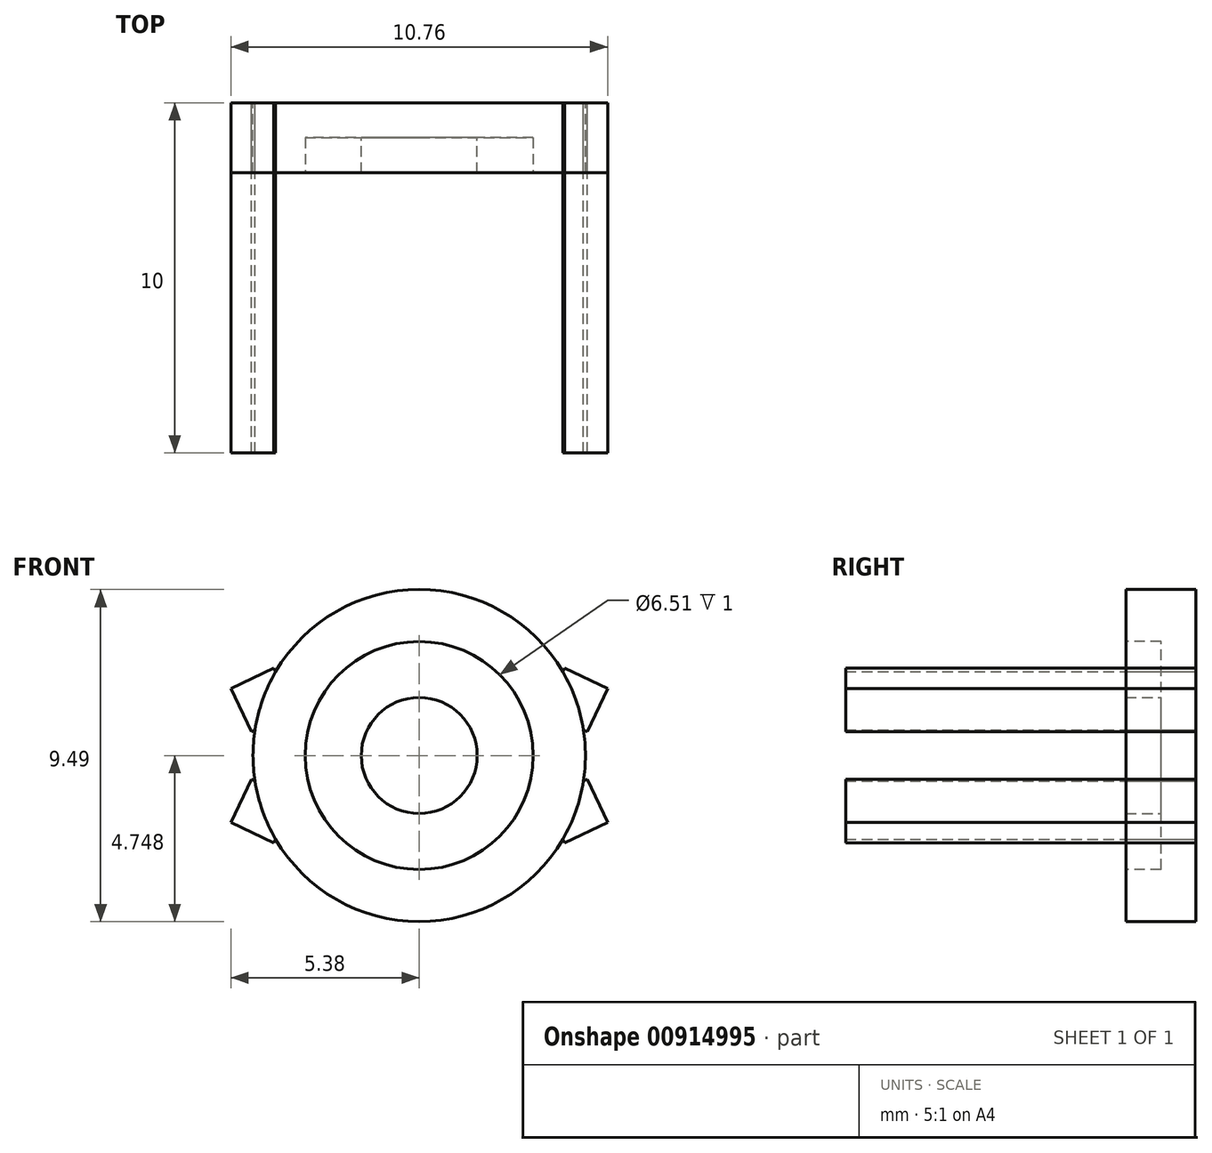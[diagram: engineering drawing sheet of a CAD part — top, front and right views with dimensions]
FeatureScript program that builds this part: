
annotation { "Feature Type Name" : "Feature", "Feature Type Description" : "" }
export const myFeature = defineFeature(function(context is Context, id is Id, definition is map)
    precondition{}
    {
        {
            var Q0;
            Q0=qCreatedBy(makeId("Front.planeOp"),FACE);
            var sketch = newSketch(context, id + "F0", { "sketchPlane" : qUnion([Q0])});
            skLineSegment(sketch, "E0", {"start": v(0, 0) * mm, "end": v(0, 1.59) * mm});
            skLineSegment(sketch, "E1", {"start": v(0, 1.59) * mm, "end": v(4.47, 0) * mm, "construction": true});
            skLineSegment(sketch, "E2", {"start": v(4.47, 0) * mm, "end": v(0, 0) * mm, "construction": true});
            skLineSegment(sketch, "E3", {"start": v(0, 1.59) * mm, "end": v(-4.47, 0) * mm, "construction": true});
            skLineSegment(sketch, "E4", {"start": v(-4.47, 0) * mm, "end": v(0, 0) * mm, "construction": true});
            skLineSegment(sketch, "E5", {"start": v(0, 1.59) * mm, "end": v(162.6, 1.59) * mm, "construction": true});
            skLineSegment(sketch, "E6.MirrorCS", {"start": v(0, 1.59) * mm, "end": v(4.47, 3.18) * mm, "construction": true});
            skLineSegment(sketch, "E7.MirrorCS", {"start": v(0, 1.59) * mm, "end": v(-4.47, 3.18) * mm, "construction": true});
            skLineSegment(sketch, "E8.MirrorCS", {"start": v(-4.47, 3.18) * mm, "end": v(0, 3.18) * mm, "construction": true});
            skLineSegment(sketch, "E9.MirrorCS", {"start": v(4.47, 3.18) * mm, "end": v(0, 3.18) * mm, "construction": true});
            skCircle(sketch, "E10", {"center": v(0, 1.59) * mm, "radius": 4.75 * mm});
            skCircle(sketch, "E11.cCircle", {"center": v(4.47, 3.18) * mm, "radius": 0.96 * mm, "construction": true});
            skLineSegment(sketch, "E11.0", {"start": v(5.38, 3.5) * mm, "end": v(4.8, 2.27) * mm});
            skLineSegment(sketch, "E11.1", {"start": v(4.8, 2.27) * mm, "end": v(3.57, 2.85) * mm});
            skLineSegment(sketch, "E11.2", {"start": v(3.57, 2.85) * mm, "end": v(4.15, 4.08) * mm});
            skLineSegment(sketch, "E11.3", {"start": v(4.15, 4.08) * mm, "end": v(5.38, 3.5) * mm});
            skCircle(sketch, "E12.cCircle", {"center": v(-4.47, 3.18) * mm, "radius": 0.96 * mm, "construction": true});
            skLineSegment(sketch, "E12.0", {"start": v(-5.38, 3.5) * mm, "end": v(-4.15, 4.08) * mm});
            skLineSegment(sketch, "E12.1", {"start": v(-4.15, 4.08) * mm, "end": v(-3.57, 2.85) * mm});
            skLineSegment(sketch, "E12.2", {"start": v(-3.57, 2.85) * mm, "end": v(-4.8, 2.27) * mm});
            skLineSegment(sketch, "E12.3", {"start": v(-4.8, 2.27) * mm, "end": v(-5.38, 3.5) * mm});
            skCircle(sketch, "E13.cCircle", {"center": v(4.47, 0) * mm, "radius": 0.96 * mm, "construction": true});
            skLineSegment(sketch, "E13.0", {"start": v(5.38, -0.32) * mm, "end": v(4.15, -0.9) * mm});
            skLineSegment(sketch, "E13.1", {"start": v(4.15, -0.9) * mm, "end": v(3.57, 0.32) * mm});
            skLineSegment(sketch, "E13.2", {"start": v(3.57, 0.32) * mm, "end": v(4.8, 0.9) * mm});
            skLineSegment(sketch, "E13.3", {"start": v(4.8, 0.9) * mm, "end": v(5.38, -0.32) * mm});
            skCircle(sketch, "E14.cCircle", {"center": v(-4.47, 0) * mm, "radius": 0.96 * mm, "construction": true});
            skLineSegment(sketch, "E14.0", {"start": v(-5.38, -0.32) * mm, "end": v(-4.8, 0.9) * mm});
            skLineSegment(sketch, "E14.1", {"start": v(-4.8, 0.9) * mm, "end": v(-3.57, 0.32) * mm});
            skLineSegment(sketch, "E14.2", {"start": v(-3.57, 0.32) * mm, "end": v(-4.15, -0.9) * mm});
            skLineSegment(sketch, "E14.3", {"start": v(-4.15, -0.9) * mm, "end": v(-5.38, -0.32) * mm});
            skLineSegment(sketch, "E15", {"start": v(-4.15, 4.08) * mm, "end": v(0, 1.59) * mm, "construction": true});
            skLineSegment(sketch, "E16", {"start": v(4.15, 4.08) * mm, "end": v(0, 1.59) * mm, "construction": true});
            skPoint(sketch, "E17", {"position": v(4.07, 4.03) * mm});
            skPoint(sketch, "E18", {"position": v(-4.07, 4.03) * mm});
            skLineSegment(sketch, "E19", {"start": v(0, 1.59) * mm, "end": v(4.15, -0.9) * mm, "construction": true});
            skLineSegment(sketch, "E20", {"start": v(0, 1.59) * mm, "end": v(-4.15, -0.9) * mm, "construction": true});
            skPoint(sketch, "E21", {"position": v(-4.07, -0.86) * mm});
            skPoint(sketch, "E22", {"position": v(4.07, -0.86) * mm});
            skLineSegment(sketch, "E23", {"start": v(-4.8, 2.27) * mm, "end": v(0, 1.59) * mm, "construction": true});
            skLineSegment(sketch, "E24", {"start": v(-4.8, 0.9) * mm, "end": v(0, 1.59) * mm, "construction": true});
            skPoint(sketch, "E25", {"position": v(-0.62, -3.12) * mm});
            skPoint(sketch, "E26", {"position": v(0.62, -3.12) * mm});
            skLineSegment(sketch, "E27", {"start": v(-0.62, -3.12) * mm, "end": v(0, 1.59) * mm, "construction": true});
            skLineSegment(sketch, "E28", {"start": v(0.62, -3.12) * mm, "end": v(0, 1.59) * mm, "construction": true});
            skPoint(sketch, "E29", {"position": v(-3.34, -1.79) * mm});
            skPoint(sketch, "E30", {"position": v(3.34, -1.79) * mm});
            skLineSegment(sketch, "E31", {"start": v(-3.34, -1.79) * mm, "end": v(0, 1.59) * mm, "construction": true});
            skLineSegment(sketch, "E32", {"start": v(3.34, -1.79) * mm, "end": v(0, 1.59) * mm, "construction": true});
            skLineSegment(sketch, "E33", {"start": v(4.8, 0.9) * mm, "end": v(0, 1.59) * mm, "construction": true});
            skSolve(sketch);
        }
        {
            var Q0;
            {var subQ3=sQuery(id+"F0.wireOp",EDGE,"E10");var subQ9=sQuery(id+"F0.wireOp",EDGE,"E11.2");var subQ12=makeQuery(id+"F0.imprint","INTERSECT",VERTEX,{"derivedFrom":[subQ3,subQ9]});Q0=makeQuery(id+"F0.imprint","IMPRINT",FACE,{"disambiguationData":[TD([[makeQuery(id+"F0.imprint","IMPRINT",EDGE,{"disambiguationData":[TD([[subQ12,-1.0]])],"derivedFrom":subQ3}),1.0]])]});}
            var Q1;
            {var subQ0=sQuery(id+"F0.wireOp",EDGE,"E12.1");var subQ1=sQuery(id+"F0.wireOp",EDGE,"E10");var subQ2=makeQuery(id+"F0.imprint","INTERSECT",VERTEX,{"derivedFrom":[subQ1,subQ0]});Q1=makeQuery(id+"F0.imprint","IMPRINT",FACE,{"disambiguationData":[TD([[makeQuery(id+"F0.imprint","IMPRINT",EDGE,{"disambiguationData":[TD([[subQ2,-1.0]])],"derivedFrom":subQ1}),1.0]])]});}
            var Q2;
            {var subQ5=sQuery(id+"F0.wireOp",EDGE,"E12.0");Q2=makeQuery(id+"F0.imprint","IMPRINT",FACE,{"disambiguationData":[TD([[makeQuery(id+"F0.imprint","IMPRINT",EDGE,{"derivedFrom":subQ5}),-1.0]])]});}
            var Q3;
            {var subQ0=sQuery(id+"F0.wireOp",EDGE,"E14.1");var subQ1=sQuery(id+"F0.wireOp",EDGE,"E10");var subQ2=makeQuery(id+"F0.imprint","INTERSECT",VERTEX,{"derivedFrom":[subQ1,subQ0]});Q3=makeQuery(id+"F0.imprint","IMPRINT",FACE,{"disambiguationData":[TD([[makeQuery(id+"F0.imprint","IMPRINT",EDGE,{"disambiguationData":[TD([[subQ2,-1.0]])],"derivedFrom":subQ1}),1.0]])]});}
            var Q4;
            {var subQ5=sQuery(id+"F0.wireOp",EDGE,"E14.0");Q4=makeQuery(id+"F0.imprint","IMPRINT",FACE,{"disambiguationData":[TD([[makeQuery(id+"F0.imprint","IMPRINT",EDGE,{"derivedFrom":subQ5}),-1.0]])]});}
            var Q5;
            {var subQ4=sQuery(id+"F0.wireOp",EDGE,"E13.0");Q5=makeQuery(id+"F0.imprint","IMPRINT",FACE,{"disambiguationData":[TD([[makeQuery(id+"F0.imprint","IMPRINT",EDGE,{"derivedFrom":subQ4}),-1.0]])]});}
            var Q6;
            {var subQ0=sQuery(id+"F0.wireOp",EDGE,"E13.1");var subQ1=sQuery(id+"F0.wireOp",EDGE,"E10");var subQ2=makeQuery(id+"F0.imprint","INTERSECT",VERTEX,{"derivedFrom":[subQ1,subQ0]});Q6=makeQuery(id+"F0.imprint","IMPRINT",FACE,{"disambiguationData":[TD([[makeQuery(id+"F0.imprint","IMPRINT",EDGE,{"disambiguationData":[TD([[subQ2,-1.0]])],"derivedFrom":subQ1}),1.0]])]});}
            var Q7;
            {var subQ0=sQuery(id+"F0.wireOp",EDGE,"E11.2");var subQ1=sQuery(id+"F0.wireOp",EDGE,"E10");var subQ2=makeQuery(id+"F0.imprint","INTERSECT",VERTEX,{"derivedFrom":[subQ1,subQ0]});Q7=makeQuery(id+"F0.imprint","IMPRINT",FACE,{"disambiguationData":[TD([[makeQuery(id+"F0.imprint","IMPRINT",EDGE,{"disambiguationData":[TD([[subQ2,1.0]])],"derivedFrom":subQ1}),1.0]])]});}
            var Q8;
            {var subQ5=sQuery(id+"F0.wireOp",EDGE,"E11.0");Q8=makeQuery(id+"F0.imprint","IMPRINT",FACE,{"disambiguationData":[TD([[makeQuery(id+"F0.imprint","IMPRINT",EDGE,{"derivedFrom":subQ5}),-1.0]])]});}
            extrude(context, id + "F1", {"entities" : qUnion([Q0, Q1, Q2, Q3, Q4, Q5, Q6, Q7, Q8]), "depth" : 2 * mm, "offsetDistance" : 25.4 * mm});
        }
        {
            var Q0;
            {var subQ5=sQuery(id+"F0.wireOp",EDGE,"E12.0");Q0=makeQuery(id+"F0.imprint","IMPRINT",FACE,{"disambiguationData":[TD([[makeQuery(id+"F0.imprint","IMPRINT",EDGE,{"derivedFrom":subQ5}),-1.0]])]});}
            var Q1;
            {var subQ5=sQuery(id+"F0.wireOp",EDGE,"E14.0");Q1=makeQuery(id+"F0.imprint","IMPRINT",FACE,{"disambiguationData":[TD([[makeQuery(id+"F0.imprint","IMPRINT",EDGE,{"derivedFrom":subQ5}),-1.0]])]});}
            var Q2;
            {var subQ4=sQuery(id+"F0.wireOp",EDGE,"E13.0");Q2=makeQuery(id+"F0.imprint","IMPRINT",FACE,{"disambiguationData":[TD([[makeQuery(id+"F0.imprint","IMPRINT",EDGE,{"derivedFrom":subQ4}),-1.0]])]});}
            var Q3;
            {var subQ5=sQuery(id+"F0.wireOp",EDGE,"E11.0");Q3=makeQuery(id+"F0.imprint","IMPRINT",FACE,{"disambiguationData":[TD([[makeQuery(id+"F0.imprint","IMPRINT",EDGE,{"derivedFrom":subQ5}),-1.0]])]});}
            extrude(context, id + "F2", {"entities" : qUnion([Q0, Q1, Q2, Q3]), "depth" : 10 * mm, "offsetDistance" : 25.4 * mm});
        }
        {
            var Q0;
            Q0=makeQuery(id+"F1.opExtrude","CAP_FACE",FACE,{"disambiguationData":[OSD([sQuery(id+"F0.wireOp",EDGE,"E10"),sQuery(id+"F0.wireOp",EDGE,"E11.0"),sQuery(id+"F0.wireOp",EDGE,"E11.1"),sQuery(id+"F0.wireOp",EDGE,"E11.2"),sQuery(id+"F0.wireOp",EDGE,"E11.3"),sQuery(id+"F0.wireOp",EDGE,"E12.0"),sQuery(id+"F0.wireOp",EDGE,"E12.1"),sQuery(id+"F0.wireOp",EDGE,"E12.2"),sQuery(id+"F0.wireOp",EDGE,"E12.3"),sQuery(id+"F0.wireOp",EDGE,"E13.0"),sQuery(id+"F0.wireOp",EDGE,"E13.1"),sQuery(id+"F0.wireOp",EDGE,"E13.2"),sQuery(id+"F0.wireOp",EDGE,"E13.3"),sQuery(id+"F0.wireOp",EDGE,"E14.0"),sQuery(id+"F0.wireOp",EDGE,"E14.1"),sQuery(id+"F0.wireOp",EDGE,"E14.2"),sQuery(id+"F0.wireOp",EDGE,"E14.3")])],"isStart":false});
            var sketch = newSketch(context, id + "F3", { "sketchPlane" : qUnion([Q0])});
            skCircle(sketch, "E34", {"center": v(0, 1.59) * mm, "radius": 3.25 * mm});
            skLineSegment(sketch, "E35", {"start": v(0, -1.67) * mm, "end": v(0, 6.33) * mm, "construction": true});
            skSolve(sketch);
        }
        {
            var Q0;
            Q0=makeQuery(id+"F3.imprint","IMPRINT",FACE,{"disambiguationData":[TD([[makeQuery(id+"F3.imprint","IMPRINT",EDGE,{"derivedFrom":sQuery(id+"F3.wireOp",EDGE,"E34")}),1.0]])]});
            extrude(context, id + "F4", {"entities" : qUnion([Q0]), "operationType" : NewBodyOperationType.REMOVE, "oppositeDirection" : true, "depth" : 1 * mm, "offsetDistance" : 25.4 * mm});
        }
        {
            var Q0;
            Q0=makeQuery(id+"F4.boolean.opBoolean","COPY",FACE,{"derivedFrom":makeQuery(id+"F4.opExtrude","CAP_FACE",FACE,{"disambiguationData":[OSD([sQuery(id+"F3.wireOp",EDGE,"E34")])],"isStart":false})});
            var sketch = newSketch(context, id + "F5", { "sketchPlane" : qUnion([Q0])});
            skCircle(sketch, "E36", {"center": v(0, 1.59) * mm, "radius": 1.65 * mm});
            skLineSegment(sketch, "E37", {"start": v(0, 3.24) * mm, "end": v(0, 4.84) * mm, "construction": true});
            skSolve(sketch);
        }
        {
            var Q0;
            Q0=makeQuery(id+"F5.imprint","IMPRINT",FACE,{"disambiguationData":[TD([[makeQuery(id+"F5.imprint","IMPRINT",EDGE,{"derivedFrom":sQuery(id+"F5.wireOp",EDGE,"E36")}),1.0]])]});
            extrude(context, id + "F6", {"entities" : qUnion([Q0]), "operationType" : NewBodyOperationType.ADD, "depth" : 1 * mm, "offsetDistance" : 25.4 * mm});
        }
    });
